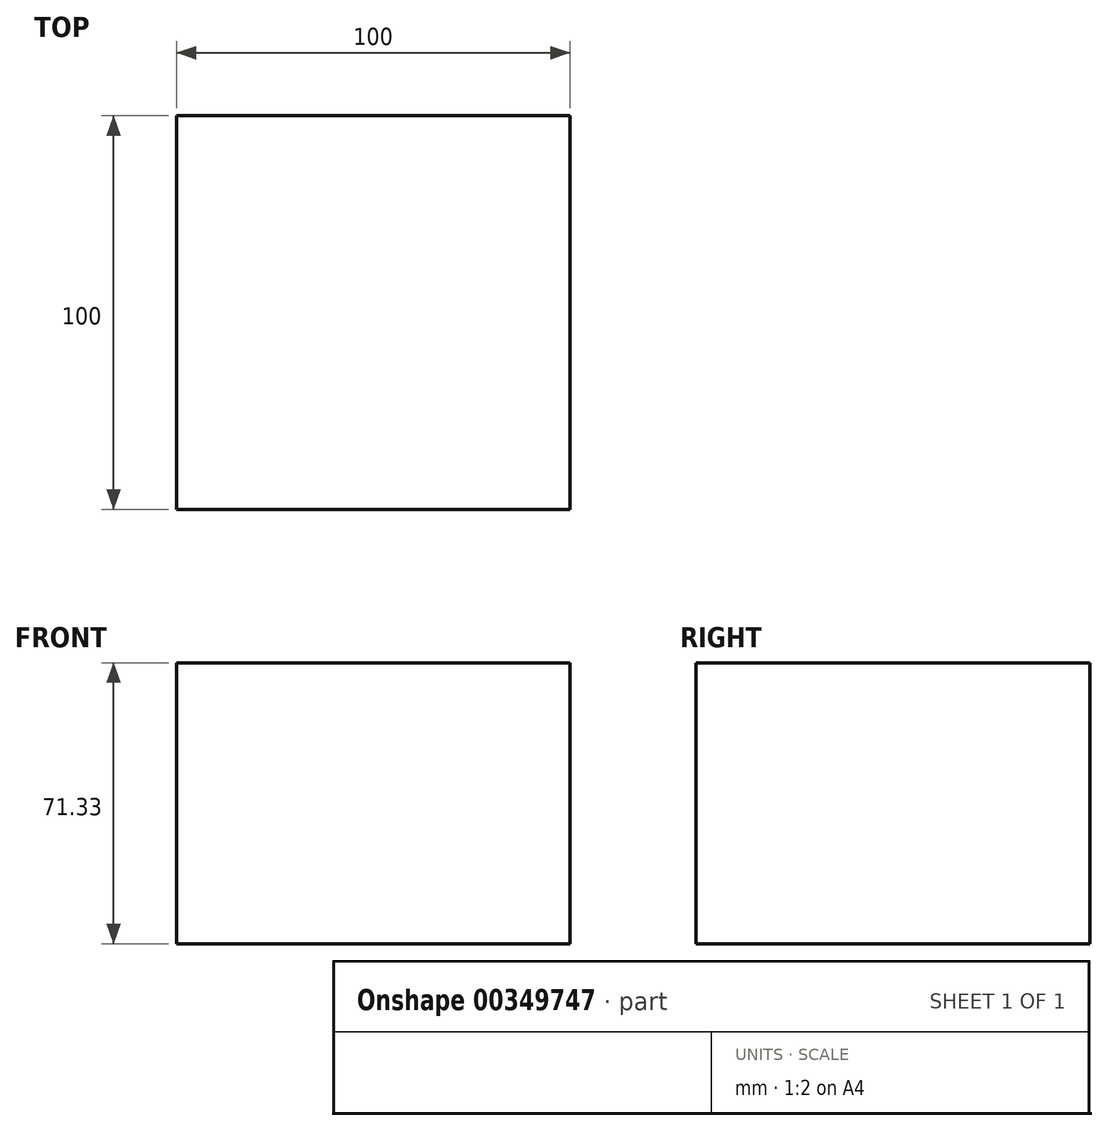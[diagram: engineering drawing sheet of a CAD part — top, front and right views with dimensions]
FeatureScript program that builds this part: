
annotation { "Feature Type Name" : "Feature", "Feature Type Description" : "" }
export const myFeature = defineFeature(function(context is Context, id is Id, definition is map)
    precondition{}
    {
        {
            var Q0;
            Q0=qCreatedBy(makeId("Right.planeOp"),FACE);
            var sketch = newSketch(context, id + "F0", { "sketchPlane" : qUnion([Q0])});
            skLineSegment(sketch, "E0.bottom", {"start": v(-49.5, -29.1) * mm, "end": v(50.5, -29.1) * mm});
            skLineSegment(sketch, "E0.top", {"start": v(-49.5, 42.23) * mm, "end": v(50.5, 42.23) * mm});
            skLineSegment(sketch, "E0.left", {"start": v(-49.5, -29.1) * mm, "end": v(-49.5, 42.23) * mm});
            skLineSegment(sketch, "E0.right", {"start": v(50.5, -29.1) * mm, "end": v(50.5, 42.23) * mm});
            skSolve(sketch);
        }
        {
            var Q0;
            Q0=makeQuery(id+"F0.imprint","IMPRINT",FACE,{"disambiguationData":[TD([[makeQuery(id+"F0.imprint","IMPRINT",EDGE,{"derivedFrom":sQuery(id+"F0.wireOp",EDGE,"E0.bottom")}),1.0]])]});
            extrude(context, id + "F1", {"entities" : qUnion([Q0]), "depth" : 100 * mm});
        }
    });
